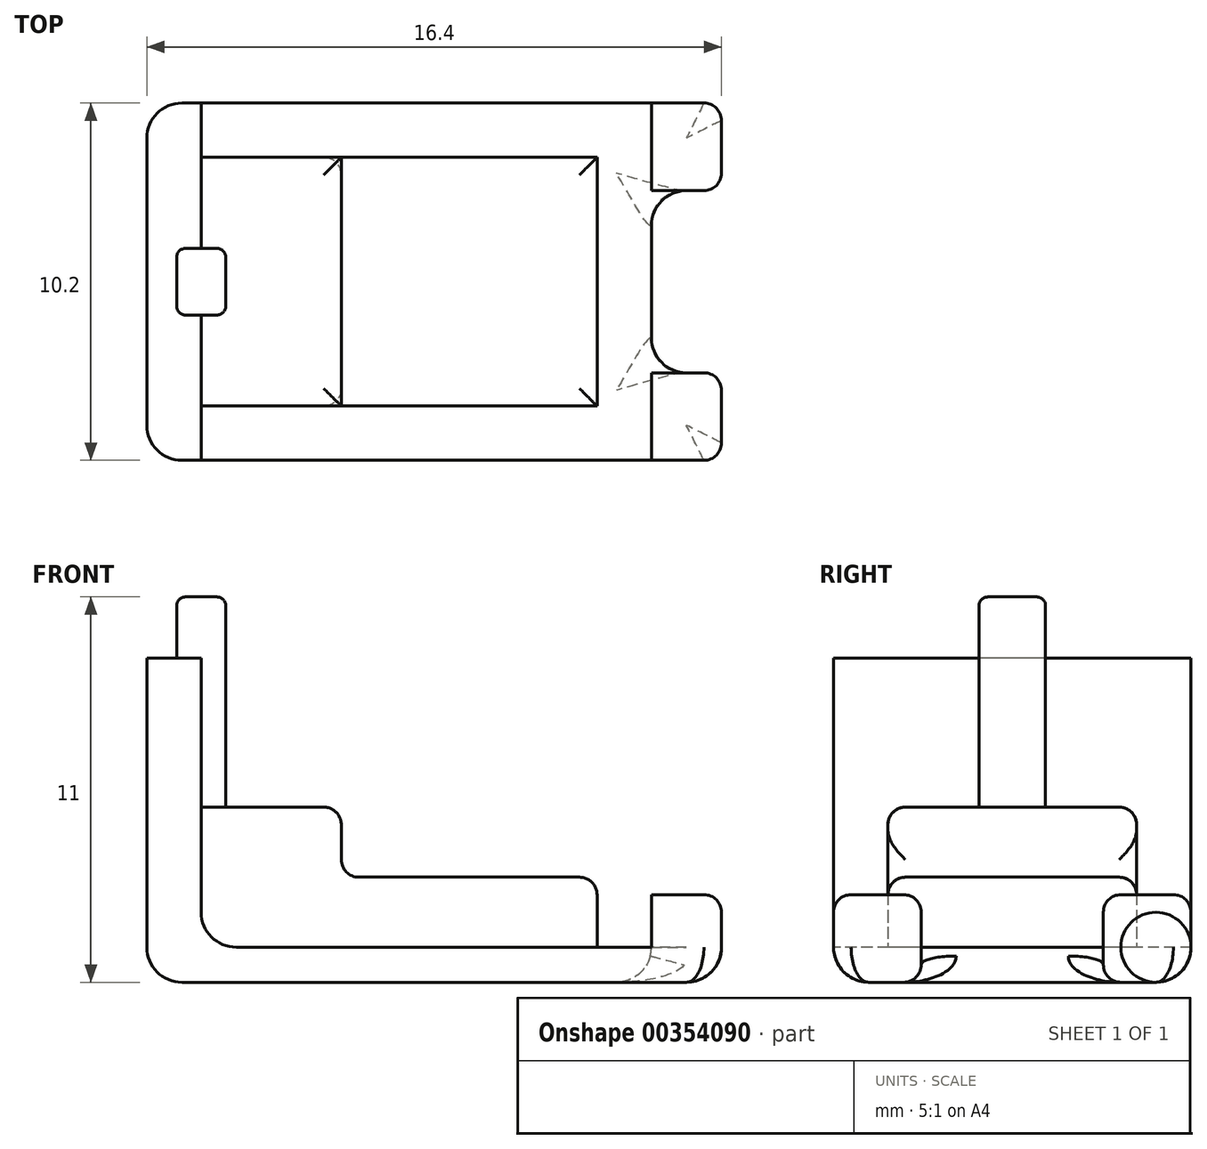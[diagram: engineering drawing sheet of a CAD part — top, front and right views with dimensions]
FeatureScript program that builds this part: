
annotation { "Feature Type Name" : "Feature", "Feature Type Description" : "" }
export const myFeature = defineFeature(function(context is Context, id is Id, definition is map)
    precondition{}
    {
        {
            var Q0;
            Q0=qCreatedBy(makeId("Top.planeOp"),FACE);
            var sketch = newSketch(context, id + "F0", { "sketchPlane" : qUnion([Q0])});
            skLineSegment(sketch, "E0.bottom", {"start": v(7.2, 5.1) * mm, "end": v(-7.2, 5.1) * mm});
            skLineSegment(sketch, "E0.top", {"start": v(7.2, -5.1) * mm, "end": v(-7.2, -5.1) * mm});
            skLineSegment(sketch, "E0.left", {"start": v(7.2, 5.1) * mm, "end": v(7.2, -5.1) * mm});
            skLineSegment(sketch, "E0.right", {"start": v(-7.2, 5.1) * mm, "end": v(-7.2, -5.1) * mm});
            skPoint(sketch, "E0.middle", {"position": v(0, 0) * mm});
            skLineSegment(sketch, "E1", {"start": v(7.2, 5.1) * mm, "end": v(7.2, 3.55) * mm, "construction": true});
            skLineSegment(sketch, "E2", {"start": v(7.2, 3.55) * mm, "end": v(5.65, 3.55) * mm, "construction": true});
            skPoint(sketch, "E3", {"position": v(5.65, 3.55) * mm});
            skPoint(sketch, "E4.MirrorP", {"position": v(-5.65, 3.55) * mm});
            skPoint(sketch, "E5.MirrorP", {"position": v(5.65, -3.55) * mm});
            skPoint(sketch, "E6.MirrorP", {"position": v(-5.65, -3.55) * mm});
            skLineSegment(sketch, "E7.bottom", {"start": v(5.65, 3.55) * mm, "end": v(-5.65, 3.55) * mm});
            skLineSegment(sketch, "E7.top", {"start": v(5.65, -3.55) * mm, "end": v(-5.65, -3.55) * mm});
            skLineSegment(sketch, "E7.left", {"start": v(5.65, 3.55) * mm, "end": v(5.65, -3.55) * mm});
            skLineSegment(sketch, "E7.right", {"start": v(-5.65, 3.55) * mm, "end": v(-5.65, -3.55) * mm});
            skLineSegment(sketch, "E8.bottom", {"start": v(-4.95, 0.95) * mm, "end": v(-6.35, 0.95) * mm});
            skLineSegment(sketch, "E8.top", {"start": v(-4.95, -0.95) * mm, "end": v(-6.35, -0.95) * mm});
            skLineSegment(sketch, "E8.left", {"start": v(-4.95, 0.95) * mm, "end": v(-4.95, -0.95) * mm});
            skLineSegment(sketch, "E8.right", {"start": v(-6.35, 0.95) * mm, "end": v(-6.35, -0.95) * mm});
            skPoint(sketch, "E8.middle", {"position": v(-5.65, 0) * mm});
            skLineSegment(sketch, "E9", {"start": v(-5.65, 0) * mm, "end": v(-1.65, 0) * mm, "construction": true});
            skLineSegment(sketch, "E10", {"start": v(-1.65, 3.55) * mm, "end": v(-1.65, -3.55) * mm});
            skLineSegment(sketch, "E11", {"start": v(-5.65, 5.1) * mm, "end": v(-5.65, -5.1) * mm});
            skLineSegment(sketch, "E12", {"start": v(7.2, 5.1) * mm, "end": v(9.2, 5.1) * mm});
            skLineSegment(sketch, "E13", {"start": v(9.2, 5.1) * mm, "end": v(9.2, 2.6) * mm});
            skLineSegment(sketch, "E14.MirrorCS", {"start": v(7.2, -5.1) * mm, "end": v(9.2, -5.1) * mm});
            skLineSegment(sketch, "E15.MirrorCS", {"start": v(9.2, -5.1) * mm, "end": v(9.2, -2.6) * mm});
            skLineSegment(sketch, "E16", {"start": v(9.2, 2.6) * mm, "end": v(7.2, 2.6) * mm});
            skLineSegment(sketch, "E17.MirrorCS", {"start": v(9.2, -2.6) * mm, "end": v(7.2, -2.6) * mm});
            skSolve(sketch);
        }
        {
            var Q0;
            Q0=makeQuery(id+"F0.imprint","IMPRINT",FACE,{"disambiguationData":[TD([[makeQuery(id+"F0.imprint","IMPRINT",EDGE,{"derivedFrom":sQuery(id+"F0.wireOp",EDGE,"E0.bottom")}),1.0]])]});
            var Q1;
            {var subQ10=sQuery(id+"F0.wireOp",EDGE,"E8.left");Q1=makeQuery(id+"F0.imprint","IMPRINT",FACE,{"disambiguationData":[TD([[makeQuery(id+"F0.imprint","IMPRINT",EDGE,{"derivedFrom":subQ10}),1.0]])]});}
            var Q2;
            {var subQ0=sQuery(id+"F0.wireOp",EDGE,"E7.left");Q2=makeQuery(id+"F0.imprint","IMPRINT",FACE,{"disambiguationData":[TD([[makeQuery(id+"F0.imprint","IMPRINT",EDGE,{"derivedFrom":subQ0}),-1.0]])]});}
            var Q3;
            {var subQ5=sQuery(id+"F0.wireOp",EDGE,"E8.left");Q3=makeQuery(id+"F0.imprint","IMPRINT",FACE,{"disambiguationData":[TD([[makeQuery(id+"F0.imprint","IMPRINT",EDGE,{"derivedFrom":subQ5}),-1.0]])]});}
            var Q4;
            {var subQ5=sQuery(id+"F0.wireOp",EDGE,"E8.right");Q4=makeQuery(id+"F0.imprint","IMPRINT",FACE,{"disambiguationData":[TD([[makeQuery(id+"F0.imprint","IMPRINT",EDGE,{"derivedFrom":subQ5}),1.0]])]});}
            var Q5;
            {var subQ0=sQuery(id+"F0.wireOp",EDGE,"E7.left");Q5=makeQuery(id+"F0.imprint","IMPRINT",FACE,{"disambiguationData":[TD([[makeQuery(id+"F0.imprint","IMPRINT",EDGE,{"derivedFrom":subQ0}),1.0]])]});}
            var Q6;
            {var subQ0=sQuery(id+"F0.wireOp",EDGE,"E14.MirrorCS");Q6=makeQuery(id+"F0.imprint","IMPRINT",FACE,{"disambiguationData":[TD([[makeQuery(id+"F0.imprint","IMPRINT",EDGE,{"derivedFrom":subQ0}),1.0]])]});}
            var Q7;
            {var subQ0=sQuery(id+"F0.wireOp",EDGE,"E12");Q7=makeQuery(id+"F0.imprint","IMPRINT",FACE,{"disambiguationData":[TD([[makeQuery(id+"F0.imprint","IMPRINT",EDGE,{"derivedFrom":subQ0}),-1.0]])]});}
            extrude(context, id + "F1", {"entities" : qUnion([Q0, Q1, Q2, Q3, Q4, Q5, Q6, Q7]), "oppositeDirection" : true, "depth" : 1 * mm});
        }
        {
            var Q0;
            {var subQ0=sQuery(id+"F0.wireOp",EDGE,"E7.left");Q0=makeQuery(id+"F0.imprint","IMPRINT",FACE,{"disambiguationData":[TD([[makeQuery(id+"F0.imprint","IMPRINT",EDGE,{"derivedFrom":subQ0}),-1.0]])]});}
            extrude(context, id + "F2", {"entities" : qUnion([Q0]), "operationType" : NewBodyOperationType.ADD, "depth" : 2 * mm});
        }
        {
            var Q0;
            {var subQ10=sQuery(id+"F0.wireOp",EDGE,"E8.left");Q0=makeQuery(id+"F0.imprint","IMPRINT",FACE,{"disambiguationData":[TD([[makeQuery(id+"F0.imprint","IMPRINT",EDGE,{"derivedFrom":subQ10}),1.0]])]});}
            extrude(context, id + "F3", {"entities" : qUnion([Q0]), "operationType" : NewBodyOperationType.ADD, "depth" : 4 * mm});
        }
        {
            var Q0;
            {var subQ4=sQuery(id+"F0.wireOp",EDGE,"E0.right");Q0=makeQuery(id+"F0.imprint","IMPRINT",FACE,{"disambiguationData":[TD([[makeQuery(id+"F0.imprint","IMPRINT",EDGE,{"derivedFrom":subQ4}),1.0]])]});}
            extrude(context, id + "F4", {"entities" : qUnion([Q0]), "operationType" : NewBodyOperationType.ADD, "depth" : 8.25 * mm});
        }
        {
            var Q0;
            {var subQ0=sQuery(id+"F0.wireOp",EDGE,"E8.left");Q0=makeQuery(id+"F0.imprint","IMPRINT",FACE,{"disambiguationData":[TD([[makeQuery(id+"F0.imprint","IMPRINT",EDGE,{"derivedFrom":subQ0}),-1.0]])]});}
            var Q1;
            {var subQ0=sQuery(id+"F0.wireOp",EDGE,"E8.right");Q1=makeQuery(id+"F0.imprint","IMPRINT",FACE,{"disambiguationData":[TD([[makeQuery(id+"F0.imprint","IMPRINT",EDGE,{"derivedFrom":subQ0}),1.0]])]});}
            extrude(context, id + "F5", {"entities" : qUnion([Q0, Q1]), "operationType" : NewBodyOperationType.ADD, "depth" : 10 * mm});
        }
        {
            var Q0;
            {var subQ0=sQuery(id+"F0.wireOp",EDGE,"E12");Q0=makeQuery(id+"F0.imprint","IMPRINT",FACE,{"disambiguationData":[TD([[makeQuery(id+"F0.imprint","IMPRINT",EDGE,{"derivedFrom":subQ0}),-1.0]])]});}
            var Q1;
            {var subQ0=sQuery(id+"F0.wireOp",EDGE,"E14.MirrorCS");Q1=makeQuery(id+"F0.imprint","IMPRINT",FACE,{"disambiguationData":[TD([[makeQuery(id+"F0.imprint","IMPRINT",EDGE,{"derivedFrom":subQ0}),1.0]])]});}
            extrude(context, id + "F6", {"entities" : qUnion([Q0, Q1]), "operationType" : NewBodyOperationType.ADD, "depth" : 1.5 * mm});
        }
        {
            var Q0;
            Q0=makeQuery(id+"F1.opExtrude","CAP_EDGE",EDGE,{"disambiguationData":[OSD([sQuery(id+"F0.wireOp",EDGE,"E0.right")])],"isStart":false});
            var Q1;
            Q1=makeQuery(id+"F1.opExtrude","CAP_EDGE",EDGE,{"disambiguationData":[OSD([sQuery(id+"F0.wireOp",EDGE,"E0.bottom"),sQuery(id+"F0.wireOp",EDGE,"E12")])],"isStart":false});
            var Q2;
            Q2=makeQuery(id+"F1.opExtrude","CAP_EDGE",EDGE,{"disambiguationData":[OSD([sQuery(id+"F0.wireOp",EDGE,"E0.top"),sQuery(id+"F0.wireOp",EDGE,"E14.MirrorCS")])],"isStart":false});
            var Q3;
            Q3=makeQuery(id+"F1.opExtrude","CAP_EDGE",EDGE,{"disambiguationData":[OSD([sQuery(id+"F0.wireOp",EDGE,"E0.left")])],"isStart":false});
            var Q4;
            Q4=makeQuery(id+"F1.opExtrude","CAP_EDGE",EDGE,{"disambiguationData":[OSD([sQuery(id+"F0.wireOp",EDGE,"E15.MirrorCS")])],"isStart":false});
            var Q5;
            Q5=makeQuery(id+"F1.opExtrude","CAP_EDGE",EDGE,{"disambiguationData":[OSD([sQuery(id+"F0.wireOp",EDGE,"E13")])],"isStart":false});
            var Q6;
            {var subQ0=sQuery(id+"F0.wireOp",EDGE,"E0.right");var subQ1=sQuery(id+"F0.wireOp",EDGE,"E0.bottom");Q6=makeQuery(id+"F4.boolean.opBoolean","MERGE",EDGE,{"derivedFrom":[makeQuery(id+"F1.opExtrude","SWEPT_EDGE",EDGE,{"disambiguationData":[OSD([subQ1,subQ0])]}),makeQuery(id+"F4.opExtrude","SWEPT_EDGE",EDGE,{"disambiguationData":[OSD([subQ1,subQ0])]})]});}
            var Q7;
            {var subQ0=sQuery(id+"F0.wireOp",EDGE,"E0.right");var subQ1=sQuery(id+"F0.wireOp",EDGE,"E0.top");Q7=makeQuery(id+"F4.boolean.opBoolean","MERGE",EDGE,{"derivedFrom":[makeQuery(id+"F1.opExtrude","SWEPT_EDGE",EDGE,{"disambiguationData":[OSD([subQ1,subQ0])]}),makeQuery(id+"F4.opExtrude","SWEPT_EDGE",EDGE,{"disambiguationData":[OSD([subQ1,subQ0])]})]});}
            fillet(context, id + "F7", {"entities" : qUnion([Q0, Q1, Q2, Q3, Q4, Q5, Q6, Q7]), "radius" : 1 * mm, "tangentPropagation" : true, "allowEdgeOverflow" : false});
        }
        {
            var Q0;
            {var subQ0=sQuery(id+"F0.wireOp",EDGE,"wnE9BAvx-uZHy-J5lG-yK8t-LQi2mgdSvlPa");Q0=makeQuery(id+"F7.opFillet","BLEND_EDGE",EDGE,{"blendedFrom":[makeQuery(id+"F1.opExtrude","CAP_EDGE",EDGE,{"disambiguationData":[OSD([sQuery(id+"F0.wireOp",EDGE,"E13")])],"isStart":false}),makeQuery(id+"F6.boolean.opBoolean","MERGE",FACE,{"derivedFrom":[makeQuery(id+"F1.opExtrude","SWEPT_FACE",FACE,{"disambiguationData":[OSD([subQ0])]}),makeQuery(id+"F6.opExtrude","SWEPT_FACE",FACE,{"disambiguationData":[OSD([subQ0])]})]})],"blendedInto":[makeQuery(id+"F6.boolean.opBoolean","MERGE",FACE,{"derivedFrom":[makeQuery(id+"F1.opExtrude","SWEPT_FACE",FACE,{"disambiguationData":[OSD([subQ0])]}),makeQuery(id+"F6.opExtrude","SWEPT_FACE",FACE,{"disambiguationData":[OSD([subQ0])]})]})]});}
            var Q1;
            Q1=makeQuery(id+"F1.opExtrude","CAP_EDGE",EDGE,{"disambiguationData":[OSD([sQuery(id+"F0.wireOp",EDGE,"wnE9BAvx-uZHy-J5lG-yK8t-LQi2mgdSvlPa")])],"isStart":false});
            var Q2;
            {var subQ0=sQuery(id+"F0.wireOp",EDGE,"a19e3a19-f6da-415a-ae3b-c89319a33e7d0.MirrorCS");Q2=makeQuery(id+"F7.opFillet","BLEND_EDGE",EDGE,{"blendedFrom":[makeQuery(id+"F1.opExtrude","CAP_EDGE",EDGE,{"disambiguationData":[OSD([sQuery(id+"F0.wireOp",EDGE,"E15.MirrorCS")])],"isStart":false}),makeQuery(id+"F6.boolean.opBoolean","MERGE",FACE,{"derivedFrom":[makeQuery(id+"F1.opExtrude","SWEPT_FACE",FACE,{"disambiguationData":[OSD([subQ0])]}),makeQuery(id+"F6.opExtrude","SWEPT_FACE",FACE,{"disambiguationData":[OSD([subQ0])]})]})],"blendedInto":[makeQuery(id+"F6.boolean.opBoolean","MERGE",FACE,{"derivedFrom":[makeQuery(id+"F1.opExtrude","SWEPT_FACE",FACE,{"disambiguationData":[OSD([subQ0])]}),makeQuery(id+"F6.opExtrude","SWEPT_FACE",FACE,{"disambiguationData":[OSD([subQ0])]})]})]});}
            var Q3;
            {var subQ0=sQuery(id+"F0.wireOp",EDGE,"E15.MirrorCS");var subQ1=sQuery(id+"F0.wireOp",EDGE,"E14.MirrorCS");Q3=makeQuery(id+"F6.boolean.opBoolean","MERGE",EDGE,{"derivedFrom":[makeQuery(id+"F1.opExtrude","SWEPT_EDGE",EDGE,{"disambiguationData":[OSD([subQ1,subQ0])]}),makeQuery(id+"F6.opExtrude","SWEPT_EDGE",EDGE,{"disambiguationData":[OSD([subQ1,subQ0])]})]});}
            var Q4;
            {var subQ0=sQuery(id+"F0.wireOp",EDGE,"E13");var subQ1=sQuery(id+"F0.wireOp",EDGE,"E12");Q4=makeQuery(id+"F6.boolean.opBoolean","MERGE",EDGE,{"derivedFrom":[makeQuery(id+"F1.opExtrude","SWEPT_EDGE",EDGE,{"disambiguationData":[OSD([subQ1,subQ0])]}),makeQuery(id+"F6.opExtrude","SWEPT_EDGE",EDGE,{"disambiguationData":[OSD([subQ1,subQ0])]})]});}
            var Q5;
            Q5=makeQuery(id+"F6.opExtrude","CAP_EDGE",EDGE,{"disambiguationData":[OSD([sQuery(id+"F0.wireOp",EDGE,"wnE9BAvx-uZHy-J5lG-yK8t-LQi2mgdSvlPa")])],"isStart":false});
            var Q6;
            Q6=makeQuery(id+"F6.opExtrude","CAP_EDGE",EDGE,{"disambiguationData":[OSD([sQuery(id+"F0.wireOp",EDGE,"E14.MirrorCS")])],"isStart":false});
            var Q7;
            Q7=makeQuery(id+"F6.opExtrude","CAP_EDGE",EDGE,{"disambiguationData":[OSD([sQuery(id+"F0.wireOp",EDGE,"E15.MirrorCS")])],"isStart":false});
            var Q8;
            Q8=makeQuery(id+"F6.opExtrude","CAP_EDGE",EDGE,{"disambiguationData":[OSD([sQuery(id+"F0.wireOp",EDGE,"E13")])],"isStart":false});
            var Q9;
            Q9=makeQuery(id+"F6.opExtrude","CAP_EDGE",EDGE,{"disambiguationData":[OSD([sQuery(id+"F0.wireOp",EDGE,"a19e3a19-f6da-415a-ae3b-c89319a33e7d0.MirrorCS")])],"isStart":false});
            var Q10;
            Q10=makeQuery(id+"F6.opExtrude","CAP_EDGE",EDGE,{"disambiguationData":[OSD([sQuery(id+"F0.wireOp",EDGE,"E12")])],"isStart":false});
            fillet(context, id + "F8", {"entities" : qUnion([Q0, Q1, Q2, Q3, Q4, Q5, Q6, Q7, Q8, Q9, Q10]), "radius" : .5 * mm, "tangentPropagation" : true, "allowEdgeOverflow" : false});
        }
        {
            var Q0;
            Q0=makeQuery(id+"F2.opExtrude","CAP_FACE",FACE,{"disambiguationData":[OSD([sQuery(id+"F0.wireOp",EDGE,"E7.bottom"),sQuery(id+"F0.wireOp",EDGE,"E7.top"),sQuery(id+"F0.wireOp",EDGE,"E7.left"),sQuery(id+"F0.wireOp",EDGE,"E10")])],"isStart":false});
            var Q1;
            Q1=makeQuery(id+"F3.opExtrude","CAP_EDGE",EDGE,{"disambiguationData":[OSD([sQuery(id+"F0.wireOp",EDGE,"E7.top")])],"isStart":false});
            var Q2;
            Q2=makeQuery(id+"F3.opExtrude","CAP_EDGE",EDGE,{"disambiguationData":[OSD([sQuery(id+"F0.wireOp",EDGE,"E7.bottom")])],"isStart":false});
            var Q3;
            Q3=makeQuery(id+"F3.opExtrude","CAP_EDGE",EDGE,{"disambiguationData":[OSD([sQuery(id+"F0.wireOp",EDGE,"E10")])],"isStart":false});
            fillet(context, id + "F9", {"entities" : qUnion([Q0, Q1, Q2, Q3]), "radius" : .5 * mm, "tangentPropagation" : true, "allowEdgeOverflow" : false});
        }
        {
            var Q0;
            {var subQ0=sQuery(id+"F0.wireOp",EDGE,"E11");var subQ1=makeQuery(id+"F0.imprint","INTERSECT",VERTEX,{"derivedFrom":[sQuery(id+"F0.wireOp",EDGE,"E7.top"),subQ0]});Q0=makeQuery(id+"F4.opExtrude","CAP_EDGE",EDGE,{"disambiguationData":[OSD([subQ0]),TDD([makeQuery(id+"F0.imprint","IMPRINT",EDGE,{"disambiguationData":[TD([[subQ1,1.0]])],"derivedFrom":subQ0}),makeQuery(id+"F0.imprint","IMPRINT",EDGE,{"disambiguationData":[TD([[subQ1,-1.0]])],"derivedFrom":subQ0})])],"isStart":true});}
            var Q1;
            {var subQ0=sQuery(id+"F0.wireOp",EDGE,"E11");var subQ1=makeQuery(id+"F0.imprint","INTERSECT",VERTEX,{"derivedFrom":[sQuery(id+"F0.wireOp",EDGE,"E7.bottom"),subQ0]});Q1=makeQuery(id+"F4.opExtrude","CAP_EDGE",EDGE,{"disambiguationData":[OSD([subQ0]),TDD([makeQuery(id+"F0.imprint","IMPRINT",EDGE,{"disambiguationData":[TD([[subQ1,1.0]])],"derivedFrom":subQ0}),makeQuery(id+"F0.imprint","IMPRINT",EDGE,{"disambiguationData":[TD([[subQ1,-1.0]])],"derivedFrom":subQ0})])],"isStart":true});}
            fillet(context, id + "F10", {"entities" : qUnion([Q0, Q1]), "radius" : 1 * mm, "tangentPropagation" : true, "allowEdgeOverflow" : false});
        }
        {
            var Q0;
            {var subQ0=sQuery(id+"F0.wireOp",EDGE,"E17.MirrorCS");var subQ1=sQuery(id+"F0.wireOp",EDGE,"E15.MirrorCS");Q0=makeQuery(id+"F6.boolean.opBoolean","MERGE",EDGE,{"derivedFrom":[makeQuery(id+"F1.opExtrude","SWEPT_EDGE",EDGE,{"disambiguationData":[OSD([subQ1,subQ0])]}),makeQuery(id+"F6.opExtrude","SWEPT_EDGE",EDGE,{"disambiguationData":[OSD([subQ1,subQ0])]})]});}
            var Q1;
            {var subQ0=sQuery(id+"F0.wireOp",EDGE,"E16");var subQ1=sQuery(id+"F0.wireOp",EDGE,"E13");Q1=makeQuery(id+"F6.boolean.opBoolean","MERGE",EDGE,{"derivedFrom":[makeQuery(id+"F1.opExtrude","SWEPT_EDGE",EDGE,{"disambiguationData":[OSD([subQ1,subQ0])]}),makeQuery(id+"F6.opExtrude","SWEPT_EDGE",EDGE,{"disambiguationData":[OSD([subQ1,subQ0])]})]});}
            fillet(context, id + "F11", {"entities" : qUnion([Q0, Q1]), "radius" : .5 * mm, "tangentPropagation" : true, "allowEdgeOverflow" : false});
        }
        {
            var Q0;
            {var subQ0=sQuery(id+"F0.wireOp",EDGE,"E16");Q0=makeQuery(id+"F7.opFillet","BLEND_EDGE",EDGE,{"blendedFrom":[makeQuery(id+"F1.opExtrude","CAP_EDGE",EDGE,{"disambiguationData":[OSD([sQuery(id+"F0.wireOp",EDGE,"E0.left")])],"isStart":false}),makeQuery(id+"F6.boolean.opBoolean","MERGE",FACE,{"derivedFrom":[makeQuery(id+"F1.opExtrude","SWEPT_FACE",FACE,{"disambiguationData":[OSD([subQ0])]}),makeQuery(id+"F6.opExtrude","SWEPT_FACE",FACE,{"disambiguationData":[OSD([subQ0])]})]})],"blendedInto":[makeQuery(id+"F6.boolean.opBoolean","MERGE",FACE,{"derivedFrom":[makeQuery(id+"F1.opExtrude","SWEPT_FACE",FACE,{"disambiguationData":[OSD([subQ0])]}),makeQuery(id+"F6.opExtrude","SWEPT_FACE",FACE,{"disambiguationData":[OSD([subQ0])]})]})]});}
            var Q1;
            {var subQ0=sQuery(id+"F0.wireOp",EDGE,"E17.MirrorCS");Q1=makeQuery(id+"F7.opFillet","BLEND_EDGE",EDGE,{"blendedFrom":[makeQuery(id+"F1.opExtrude","CAP_EDGE",EDGE,{"disambiguationData":[OSD([sQuery(id+"F0.wireOp",EDGE,"E0.left")])],"isStart":false}),makeQuery(id+"F6.boolean.opBoolean","MERGE",FACE,{"derivedFrom":[makeQuery(id+"F1.opExtrude","SWEPT_FACE",FACE,{"disambiguationData":[OSD([subQ0])]}),makeQuery(id+"F6.opExtrude","SWEPT_FACE",FACE,{"disambiguationData":[OSD([subQ0])]})]})],"blendedInto":[makeQuery(id+"F6.boolean.opBoolean","MERGE",FACE,{"derivedFrom":[makeQuery(id+"F1.opExtrude","SWEPT_FACE",FACE,{"disambiguationData":[OSD([subQ0])]}),makeQuery(id+"F6.opExtrude","SWEPT_FACE",FACE,{"disambiguationData":[OSD([subQ0])]})]})]});}
            fillet(context, id + "F12", {"entities" : qUnion([Q0, Q1]), "radius" : 1 * mm, "tangentPropagation" : true, "allowEdgeOverflow" : false});
        }
        {
            var Q0;
            Q0=makeQuery(id+"F5.opExtrude","CAP_FACE",FACE,{"disambiguationData":[OSD([sQuery(id+"F0.wireOp",EDGE,"E8.bottom"),sQuery(id+"F0.wireOp",EDGE,"E8.top"),sQuery(id+"F0.wireOp",EDGE,"E8.left"),sQuery(id+"F0.wireOp",EDGE,"E8.right")])],"isStart":false});
            var Q1;
            Q1=makeQuery(id+"F5.opExtrude","SWEPT_EDGE",EDGE,{"disambiguationData":[OSD([sQuery(id+"F0.wireOp",EDGE,"E8.bottom"),sQuery(id+"F0.wireOp",EDGE,"E8.left")])]});
            var Q2;
            Q2=makeQuery(id+"F5.opExtrude","SWEPT_EDGE",EDGE,{"disambiguationData":[OSD([sQuery(id+"F0.wireOp",EDGE,"E8.top"),sQuery(id+"F0.wireOp",EDGE,"E8.left")])]});
            var Q3;
            Q3=makeQuery(id+"F5.opExtrude","SWEPT_EDGE",EDGE,{"disambiguationData":[OSD([sQuery(id+"F0.wireOp",EDGE,"E8.bottom"),sQuery(id+"F0.wireOp",EDGE,"E8.right")])]});
            var Q4;
            Q4=makeQuery(id+"F5.opExtrude","SWEPT_EDGE",EDGE,{"disambiguationData":[OSD([sQuery(id+"F0.wireOp",EDGE,"E8.top"),sQuery(id+"F0.wireOp",EDGE,"E8.right")])]});
            fillet(context, id + "F13", {"entities" : qUnion([Q0, Q1, Q2, Q3, Q4]), "radius" : .25 * mm, "tangentPropagation" : true, "allowEdgeOverflow" : false});
        }
    });
